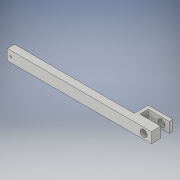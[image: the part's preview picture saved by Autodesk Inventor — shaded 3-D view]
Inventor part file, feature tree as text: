
AUTODESK INVENTOR PART (.ipt)
format: ipt  version: 2019 (Build 230136000, 136)  size: 125,440 bytes
history: native  units: in
note: dims shown in document units (in); Inventor stores cm internally (conversion verified against a paired STEP export)
features: sketch x3, hole x2, extrude x1
ambient origin geometry x8: Origin, YZ Plane, XZ Plane, XY Plane, X Axis, Y Axis, Z Axis, Center Point
bodies: Solid1 (feature_tree)
feature tree (6):
  extrude  "Extrusion1"  Depth=1.0in
  hole  "Hole1"  [1 undecoded]
  hole  "Hole2"  [1 undecoded]
  sketch  "Sketch1"  dims[d9=1.75in d10=1.0in]
  sketch  "Sketch2"  dims[d17=10.3in d24=1.525in]
  sketch  "Sketch3"  dims[d26=0.6in d27=0.25in d28=0.75in d29=0.0in d30=0.505in d31=0.75in d32=0.375in d33=0.25in d34=0.5635in d35=1.0in d36=0.8108in d37=0.55in d38=0.75in d39=0.375in d40=0.135in d41=0.75in d42=0.375in d43=0.25in d44=0.5635in d45=1.0in d46=0.8108in d47=0.75in d48=0.375in d49=0.25in d50=8.55in d51=0.25in]
note: 2 required parameter values undecoded (feature->parameter linkage not recoverable at this tier; creation-order binding heuristic only, values carry confidence <= 0.55)
